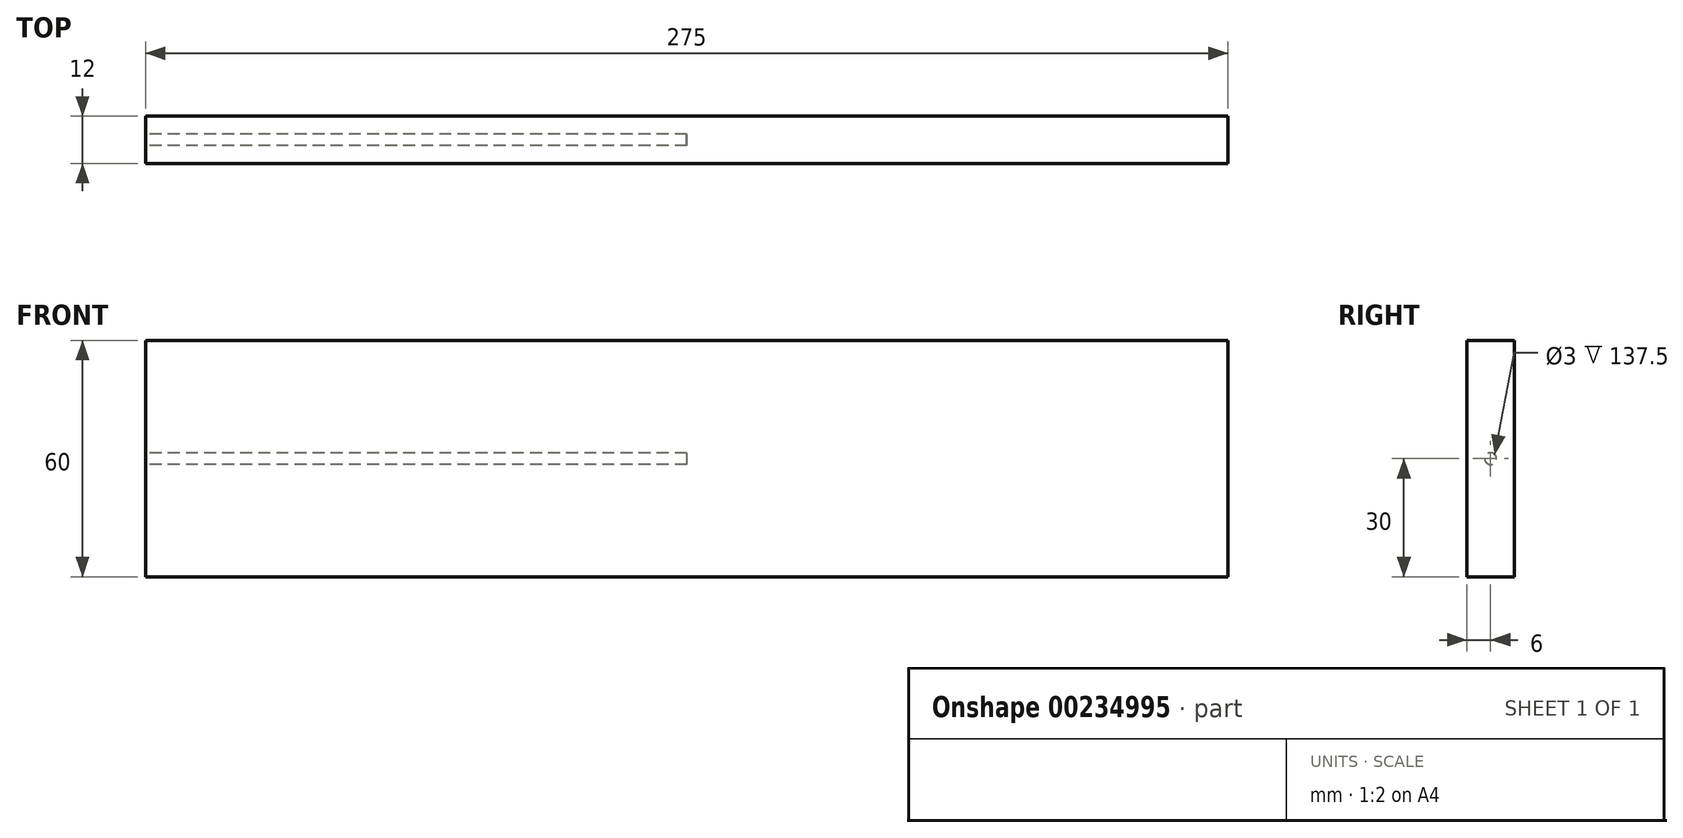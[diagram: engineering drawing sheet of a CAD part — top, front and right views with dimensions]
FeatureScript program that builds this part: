
annotation { "Feature Type Name" : "Feature", "Feature Type Description" : "" }
export const myFeature = defineFeature(function(context is Context, id is Id, definition is map)
    precondition{}
    {
        {
            var Q0;
            Q0=qCreatedBy(makeId("Front.planeOp"),FACE);
            var sketch = newSketch(context, id + "F0", { "sketchPlane" : qUnion([Q0])});
            skLineSegment(sketch, "E0.bottom", {"start": v(137.5, -30) * mm, "end": v(-137.5, -30) * mm});
            skLineSegment(sketch, "E0.top", {"start": v(137.5, 30) * mm, "end": v(-137.5, 30) * mm});
            skLineSegment(sketch, "E0.left", {"start": v(137.5, -30) * mm, "end": v(137.5, 30) * mm});
            skLineSegment(sketch, "E0.right", {"start": v(-137.5, -30) * mm, "end": v(-137.5, 30) * mm});
            skPoint(sketch, "E0.middle", {"position": v(0, 0) * mm});
            skSolve(sketch);
        }
        {
            var Q0;
            Q0 = qSketchRegion(id + "F0", true);
            extrude(context, id + "F1", {"entities" : qUnion([Q0]), "endBound" : BoundingType.SYMMETRIC, "depth" : 12 * mm});
        }
        {
            var Q0;
            Q0=makeQuery(id+"F1.opExtrude","SWEPT_FACE",FACE,{"disambiguationData":[OSD([sQuery(id+"F0.wireOp",EDGE,"E0.right")])]});
            var sketch = newSketch(context, id + "F2", { "sketchPlane" : qUnion([Q0])});
            skCircle(sketch, "E1", {"center": v(0, 0) * mm, "radius": 1.5 * mm});
            skSolve(sketch);
        }
        {
            var Q0;
            Q0 = qSketchRegion(id + "F2", true);
            extrude(context, id + "F3", {"entities" : qUnion([Q0]), "operationType" : NewBodyOperationType.REMOVE, "oppositeDirection" : true, "depth" : (275 / 2) * mm});
        }
    });
